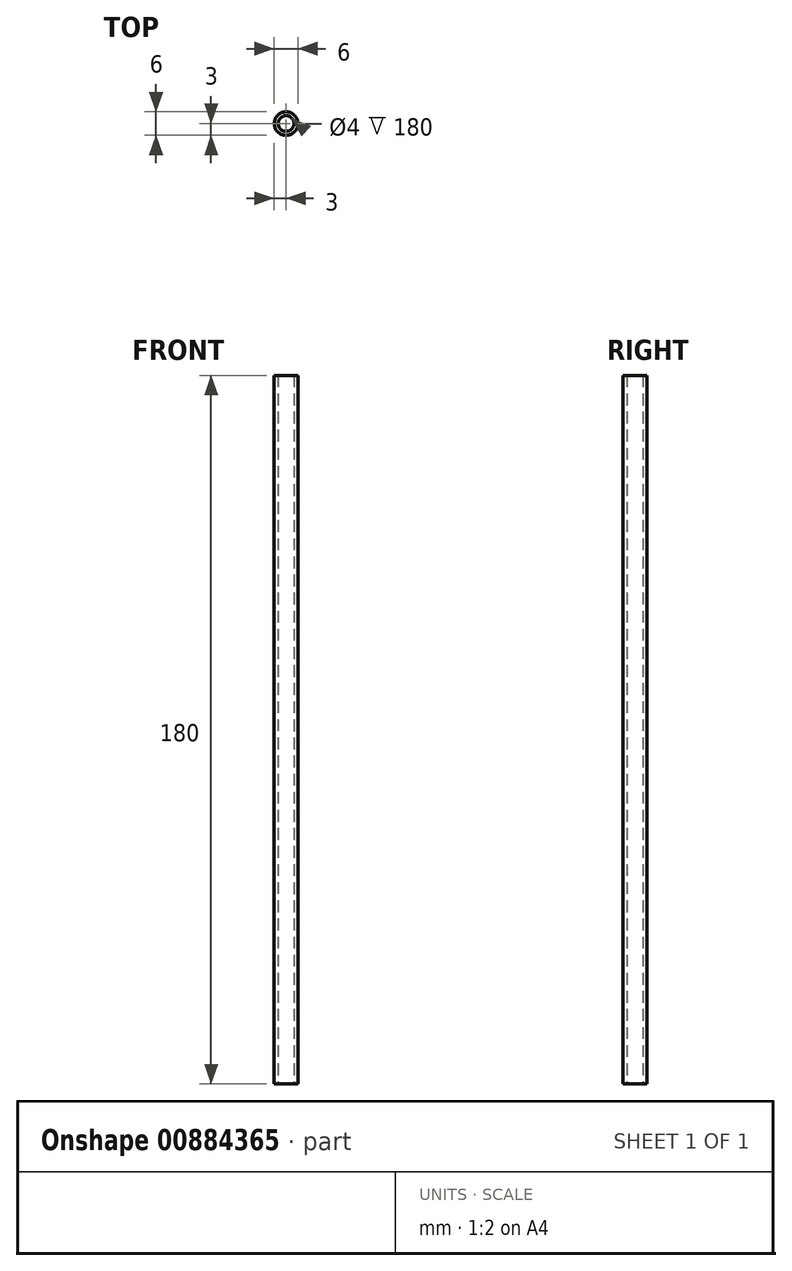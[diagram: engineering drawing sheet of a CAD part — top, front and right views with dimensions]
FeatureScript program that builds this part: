
annotation { "Feature Type Name" : "Feature", "Feature Type Description" : "" }
export const myFeature = defineFeature(function(context is Context, id is Id, definition is map)
    precondition{}
    {
        {
            var Q0;
            Q0=qCreatedBy(makeId("Top.planeOp"),FACE);
            var sketch = newSketch(context, id + "F0", { "sketchPlane" : qUnion([Q0])});
            skCircle(sketch, "E0", {"center": v(0, 0) * mm, "radius": 2 * mm});
            skCircle(sketch, "E1", {"center": v(0, 0) * mm, "radius": 3 * mm});
            skSolve(sketch);
        }
        {
            var Q0;
            Q0 = qSketchRegion(id + "F0", true);
            extrude(context, id + "F1", {"entities" : qUnion([Q0]), "depth" : 180 * mm, "offsetDistance" : 25 * mm});
        }
    });
